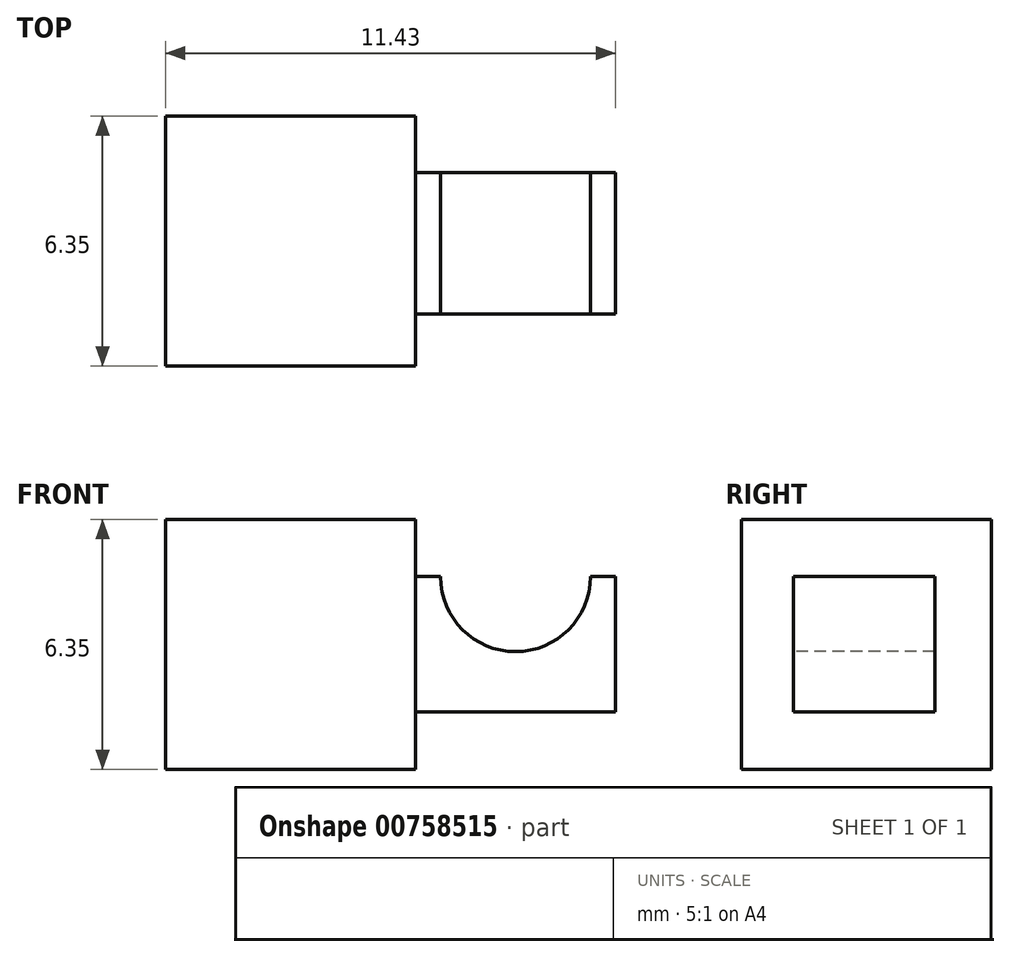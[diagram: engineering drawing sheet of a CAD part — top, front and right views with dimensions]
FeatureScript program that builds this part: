
annotation { "Feature Type Name" : "Feature", "Feature Type Description" : "" }
export const myFeature = defineFeature(function(context is Context, id is Id, definition is map)
    precondition{}
    {
        {
            var Q0;
            Q0=qCreatedBy(makeId("Right.planeOp"),FACE);
            var sketch = newSketch(context, id + "F0", { "sketchPlane" : qUnion([Q0])});
            skLineSegment(sketch, "E0.bottom", {"start": v(-41.99, 0) * mm, "end": v(-35.64, 0) * mm});
            skLineSegment(sketch, "E0.top", {"start": v(-41.99, 6.35) * mm, "end": v(-35.64, 6.35) * mm});
            skLineSegment(sketch, "E0.left", {"start": v(-41.99, 0) * mm, "end": v(-41.99, 6.35) * mm});
            skLineSegment(sketch, "E0.right", {"start": v(-35.64, 0) * mm, "end": v(-35.64, 6.35) * mm});
            skSolve(sketch);
        }
        {
            var Q0;
            Q0=makeQuery(id+"F0.imprint","IMPRINT",FACE,{"disambiguationData":[TD([[makeQuery(id+"F0.imprint","IMPRINT",EDGE,{"derivedFrom":sQuery(id+"F0.wireOp",EDGE,"E0.bottom")}),1.0]])]});
            extrude(context, id + "F1", {"entities" : qUnion([Q0]), "depth" : 6.35 * mm, "offsetDistance" : 25.4 * mm});
        }
        {
            var Q0;
            Q0=makeQuery(id+"F1.opExtrude","CAP_FACE",FACE,{"disambiguationData":[OSD([sQuery(id+"F0.wireOp",EDGE,"E0.bottom"),sQuery(id+"F0.wireOp",EDGE,"E0.top"),sQuery(id+"F0.wireOp",EDGE,"E0.left"),sQuery(id+"F0.wireOp",EDGE,"E0.right")])],"isStart":false});
            var sketch = newSketch(context, id + "F2", { "sketchPlane" : qUnion([Q0])});
            skLineSegment(sketch, "E1.bottom", {"start": v(-40.67, 1.46) * mm, "end": v(-37.08, 1.46) * mm});
            skLineSegment(sketch, "E1.top", {"start": v(-40.67, 4.9) * mm, "end": v(-37.08, 4.9) * mm});
            skLineSegment(sketch, "E1.left", {"start": v(-40.67, 1.46) * mm, "end": v(-40.67, 4.9) * mm});
            skLineSegment(sketch, "E1.right", {"start": v(-37.08, 1.46) * mm, "end": v(-37.08, 4.9) * mm});
            skSolve(sketch);
        }
        {
            var Q0;
            Q0=makeQuery(id+"F2.imprint","IMPRINT",FACE,{"disambiguationData":[TD([[makeQuery(id+"F2.imprint","IMPRINT",EDGE,{"derivedFrom":sQuery(id+"F2.wireOp",EDGE,"E1.bottom")}),1.0]])]});
            extrude(context, id + "F3", {"entities" : qUnion([Q0]), "operationType" : NewBodyOperationType.ADD, "depth" : 2.54 * mm, "offsetDistance" : 25.4 * mm});
        }
        {
            var Q0;
            Q0=makeQuery(id+"F3.opExtrude","CAP_FACE",FACE,{"disambiguationData":[OSD([sQuery(id+"F2.wireOp",EDGE,"E1.bottom"),sQuery(id+"F2.wireOp",EDGE,"E1.top"),sQuery(id+"F2.wireOp",EDGE,"E1.left"),sQuery(id+"F2.wireOp",EDGE,"E1.right")])],"isStart":false});
            var sketch = newSketch(context, id + "F4", { "sketchPlane" : qUnion([Q0])});
            skLineSegment(sketch, "E2.bottom", {"start": v(-40.67, 1.46) * mm, "end": v(-37.08, 1.46) * mm});
            skLineSegment(sketch, "E2.top", {"start": v(-40.67, 4.9) * mm, "end": v(-37.08, 4.9) * mm});
            skLineSegment(sketch, "E2.left", {"start": v(-40.67, 1.46) * mm, "end": v(-40.67, 4.9) * mm});
            skLineSegment(sketch, "E2.right", {"start": v(-37.08, 1.46) * mm, "end": v(-37.08, 4.9) * mm});
            skSolve(sketch);
        }
        {
            var Q0;
            Q0=makeQuery(id+"F4.imprint","IMPRINT",FACE,{"disambiguationData":[TD([[makeQuery(id+"F4.imprint","IMPRINT",EDGE,{"derivedFrom":sQuery(id+"F4.wireOp",EDGE,"E2.bottom")}),1.0]])]});
            extrude(context, id + "F5", {"entities" : qUnion([Q0]), "operationType" : NewBodyOperationType.ADD, "depth" : 2.54 * mm, "offsetDistance" : 25.4 * mm});
        }
        {
            var Q0;
            Q0=makeQuery(id+"F5.boolean.opBoolean","MERGE",FACE,{"derivedFrom":[makeQuery(id+"F3.opExtrude","SWEPT_FACE",FACE,{"disambiguationData":[OSD([sQuery(id+"F2.wireOp",EDGE,"E1.left")])]}),makeQuery(id+"F5.opExtrude","SWEPT_FACE",FACE,{"disambiguationData":[OSD([sQuery(id+"F4.wireOp",EDGE,"E2.left")])]})]});
            var sketch = newSketch(context, id + "F6", { "sketchPlane" : qUnion([Q0])});
            skCircle(sketch, "E3", {"center": v(8.9, 4.9) * mm, "radius": 1.84 * mm});
            skSolve(sketch);
        }
        {
            var Q0;
            Q0=sQuery(id+"F6.wireOp",VERTEX,"E3.center");
            var Q1;
            Q1=makeQuery(id+"F1.opExtrude","SWEPT_BODY",BODY,{"disambiguationData":[OSD([sQuery(id+"F0.wireOp",EDGE,"E0.bottom"),sQuery(id+"F0.wireOp",EDGE,"E0.top"),sQuery(id+"F0.wireOp",EDGE,"E0.left"),sQuery(id+"F0.wireOp",EDGE,"E0.right")])]});
            hole(context, id + "F7", {"style" : HoleStyle.SIMPLE, "endStyle" : HoleEndStyle.THROUGH, "holeDiameter" : 3.8 * mm, "majorDiameter" : 6.35 * mm, "isTappedThrough" : true, "tappedDepth" : 12.7 * mm, "tapClearance" : 3, "locations" : qUnion([Q0]), "scope" : qUnion([Q1])});
        }
    });
